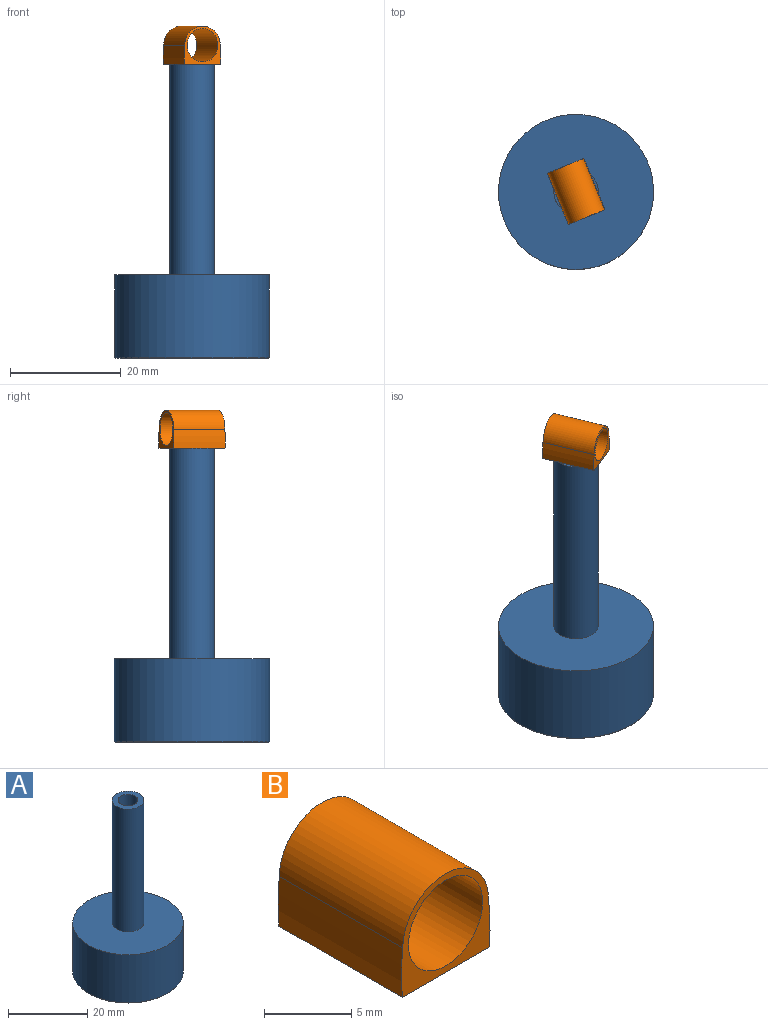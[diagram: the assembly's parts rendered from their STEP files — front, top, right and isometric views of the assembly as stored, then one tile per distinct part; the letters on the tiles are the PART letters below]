
ASSEMBLY  parts=2 mates=1
PART A: 8 faces, bbox 30.3x30.3x53 mm
  f0: cylinder r=14mm len=28mm, axis (0,0,-1), area 1310.7mm2, adj f1,f3
  f1: plane 28x28mm, normal (0,0,1), area 565.5mm2, adj f0,f5
  f2: plane 27.8x27.8mm, normal (0,0,-1), area 607mm2, adj f3
  f3: torus R=13.9mm, axis (0,0,1), area 13.8mm2, adj f0,f2
  f4: cylinder r=2.5mm len=38mm, axis (0,0,-1), area 596.9mm2, adj f6,f7
  f5: cylinder r=4mm len=38mm, axis (0,0,-1), area 955mm2, adj f1,f6
  f6: plane 8x8mm, normal (0,0,1), area 30.6mm2, adj f4,f5
  f7: plane 5x5mm, normal (0,0,1), area 19.6mm2, adj f4
PART B: 7 faces, bbox 7.2x10x6.9 mm
  f0: cylinder r=13.4mm len=10mm, axis (0,1,0), area 34.7mm2, adj f1,f4,f5,f6
  f1: cylinder r=3.46mm len=10mm, axis (0,1,0), area 108.8mm2, adj f0,f2,f5,f6
  f2: cylinder r=15.93mm len=10mm, axis (0,1,0), area 34.7mm2, adj f1,f4,f5,f6
  f3: cylinder r=3mm len=10mm, axis (0,1,0), area 188.7mm2, adj f5,f6
  f4: plane 10x7.01mm, normal (0,0,-1), area 70.1mm2, adj f0,f2,f5,f6
  f5: plane 7.18x6.93mm, normal (0,-1,0), area 15.1mm2, adj f0,f1,f2,f3,f4
  f6: plane 7.18x6.93mm, normal (0,1,0), area 15.1mm2, adj f0,f1,f2,f3,f4
PLACE A rot(axis=(0,0,1),95.1deg) t=(-11.5,90.8,-28.75)mm
PLACE B rot(axis=(0,0,1),22.3deg) t=(-11.51,90.79,-28.76)mm
MATE planar B.f4 <-> A.f0  axis (0,0,-1) through (-11.5,90.8,16.75)mm
